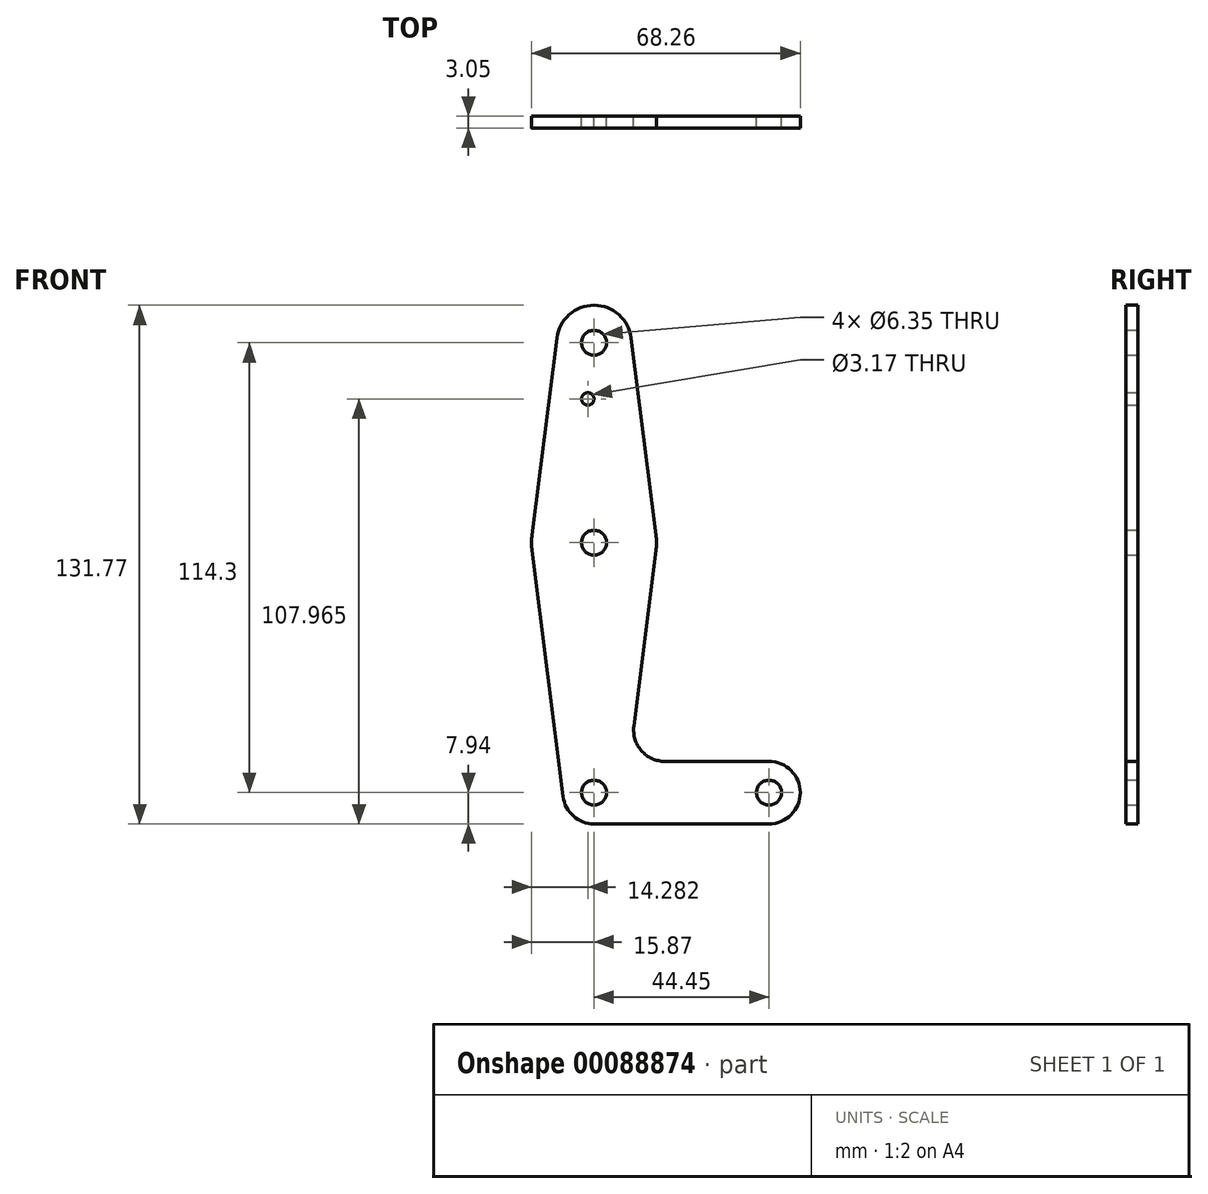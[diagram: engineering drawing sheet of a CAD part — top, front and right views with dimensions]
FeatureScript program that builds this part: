
annotation { "Feature Type Name" : "Feature", "Feature Type Description" : "" }
export const myFeature = defineFeature(function(context is Context, id is Id, definition is map)
    precondition{}
    {
        {
            var Q0;
            Q0=qCreatedBy(makeId("Front.planeOp"),FACE);
            var sketch = newSketch(context, id + "F0", { "sketchPlane" : qUnion([Q0])});
            skCircle(sketch, "E0", {"center": v(0, 114.3) * mm, "radius": 9.53 * mm});
            skCircle(sketch, "E1", {"center": v(0, 63.5) * mm, "radius": 15.88 * mm});
            skCircle(sketch, "E2", {"center": v(0, 0) * mm, "radius": 7.94 * mm});
            skCircle(sketch, "E3", {"center": v(44.45, 0) * mm, "radius": 7.94 * mm});
            skLineSegment(sketch, "E4", {"start": v(0, 114.3) * mm, "end": v(0, 0) * mm, "construction": true});
            skLineSegment(sketch, "E5", {"start": v(0, 0) * mm, "end": v(44.45, 0) * mm, "construction": true});
            skLineSegment(sketch, "E6", {"start": v(-9.45, 115.5) * mm, "end": v(-15.75, 65.48) * mm});
            skLineSegment(sketch, "E7", {"start": v(9.45, 115.5) * mm, "end": v(15.75, 65.48) * mm});
            skCircle(sketch, "E8", {"center": v(-1.59, 100.03) * mm, "radius": 1.59 * mm});
            skCircle(sketch, "E9", {"center": v(0, 114.3) * mm, "radius": 3.18 * mm});
            skCircle(sketch, "E10", {"center": v(0, 63.5) * mm, "radius": 3.18 * mm});
            skCircle(sketch, "E11", {"center": v(0, 0) * mm, "radius": 3.18 * mm});
            skCircle(sketch, "E12", {"center": v(44.45, 0) * mm, "radius": 3.18 * mm});
            skLineSegment(sketch, "E13", {"start": v(-15.75, 61.52) * mm, "end": v(-7.88, -1) * mm});
            skLineSegment(sketch, "E14", {"start": v(0, -7.94) * mm, "end": v(44.45, -7.94) * mm});
            skLineSegment(sketch, "E15", {"start": v(15.75, 61.52) * mm, "end": v(10.13, 16.88) * mm});
            skLineSegment(sketch, "E16", {"start": v(18.01, 7.94) * mm, "end": v(44.45, 7.94) * mm});
            skPoint(sketch, "E17.newPointA", {"position": v(8, 0) * mm});
            skArc(sketch, "E17.filletArc", {"start": v(10.13, 16.88) * mm, "mid": v(12.05, 10.63) * mm, "end": v(18.01, 7.94) * mm});
            skSolve(sketch);
        }
        {
            var Q0;
            Q0 = qSketchRegion(id + "F0", true);
            extrude(context, id + "F1", {"entities" : qUnion([Q0]), "depth" : 3.05 * mm});
        }
    });
